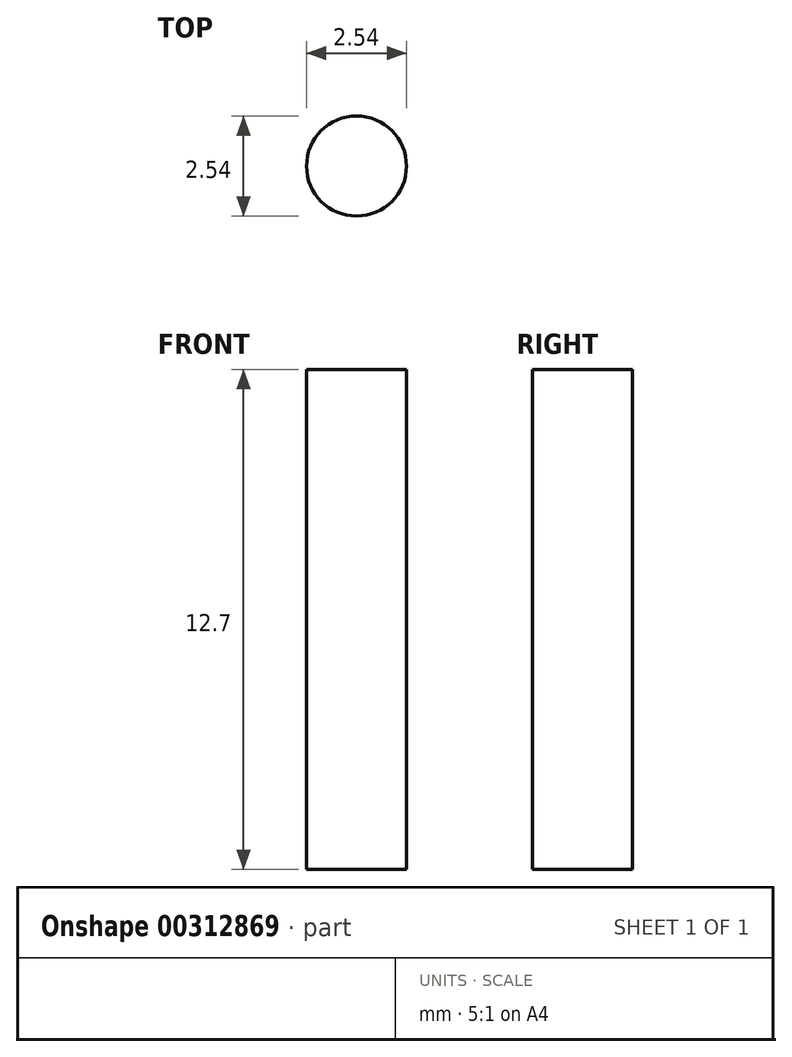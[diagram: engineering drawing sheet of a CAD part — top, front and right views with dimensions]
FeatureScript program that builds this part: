
annotation { "Feature Type Name" : "Feature", "Feature Type Description" : "" }
export const myFeature = defineFeature(function(context is Context, id is Id, definition is map)
    precondition{}
    {
        {
            var Q0;
            Q0=qCreatedBy(makeId("Front.planeOp"),FACE);
            var sketch = newSketch(context, id + "F0", { "sketchPlane" : qUnion([Q0])});
            skLineSegment(sketch, "E0", {"start": v(0, 7.99) * mm, "end": v(-1.27, 7.99) * mm});
            skLineSegment(sketch, "E1", {"start": v(-1.27, 7.99) * mm, "end": v(-1.27, -4.71) * mm});
            skLineSegment(sketch, "E2", {"start": v(-1.27, -4.71) * mm, "end": v(0, -4.71) * mm});
            skLineSegment(sketch, "E3", {"start": v(0, 12.09) * mm, "end": v(0, -10.76) * mm});
            skSolve(sketch);
        }
        {
            var Q0;
            {var subQ0=sQuery(id+"F0.wireOp",EDGE,"E0");Q0=makeQuery(id+"F0.imprint","IMPRINT",FACE,{"disambiguationData":[TD([[makeQuery(id+"F0.imprint","IMPRINT",EDGE,{"derivedFrom":subQ0}),1.0]])]});}
            var Q1;
            Q1=sQuery(id+"F0.wireOp",EDGE,"E3");
            revolve(context, id + "F1", {"entities" : qUnion([Q0]), "axis" : qUnion([Q1]), "revolveType" : RevolveType.FULL});
        }
    });
